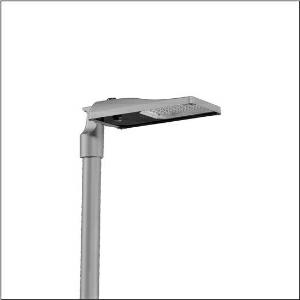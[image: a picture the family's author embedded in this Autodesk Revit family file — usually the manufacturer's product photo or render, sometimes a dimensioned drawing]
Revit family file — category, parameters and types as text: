
# Revit family: streetlight_sl_31_mini___st1_0a_5xh2d3at08ha_b443
name_source: partatom
category: Lighting Fixtures
units: mm (PartAtom-declared; Revit-internal decimal feet)

## family parameters
Cut with Voids When Loaded = No
Host = Face
Light Source = No
Part Type = Normal
Room Calculation Point = No
Round Connector Dimension = Use Diameter
Shared = No

## types (1)
- --- (1 x LED, 9230 lm, 68.3 W, 3000K)
    Apparent Load = 68 VA
    CIE Flux Codes = 37 72 97 100 100
    Color Rendering = 70
    Color Temperature = 3000K
    Default Elevation = 1800 mm
    Description = Streetlight SL 31 mini D4i mast luminaire for post-top, side-entry; light control with lens of PMMA; light distribution: ST1.0a, direct asymmetric distribution, for standard-compliant lighting for roads and squares; LED: luminous flux: 9.230lm, light colour: 730, colour temperature: 3000K; luminous efficacy: 135,1lm/W; control: pre-setting: logarithmic dimming characteristic, flexible luminous flux parameterisation, time-dependent luminous flux control, constant luminous flux control, power reduction, intelligent temperature release in ECG and LED module, overheat protection; luminaire housing, of diecast aluminium, SITECO metallic grey (DB 702S), corrosivity category C5 high according to DIN EN ISO 12944; cover of toughened safety glass, transparent, mast flange of diecast aluminium, SITECO metallic grey (DB 702S), spigot size: 76/60mm, mast flange included unmounted; cable length: 8,5m, connection cable pre-assembled; mains connection: 220..240V, AC, 50/60Hz; power consumption (at start of service life): 68,3W / (at end of service life): 74,5W / (with reduced operation 50%): 29,5W; protection rating (complete): IP66; insulation class (complete): insulation class II (safety insulation); impact resistance: IK09; certification: CE, ENEC, ENEC+, VDE, UKCA, ZD4i; permissible operating ambient temperature for outdoor applications: -40..+50°C; packaging unit: 1 piece

Light Distribution: ST1.0a
    Height = 76 mm
    Lamp = 1 x LED
    Lamp Light Flux = 9230 lm
    Lamp Power = 68.3 W
    Lamp count = 1
    Length = 547 mm
    Luminous efficacy = 135 lm/W
    Manufacturer = Siteco
    ModVariant = No
    Model = 5XH2D3AT08HA
    Number of Poles = 1
    OnlyDefault = Yes
    Power Factor = 1
    Product Name = Streetlight SL 31 mini | ST1.0a
    Product group = mast luminaire | pylon top
    ProductGroupID = 6100
    Protection Class = Protection class II
    Protection Degree = IP 66
    RLX_Detail_Level = 1
    RLX_Emergency_Light_Flux = 0 lm
    RLX_Emergency_Type = 0
    RLX_Emergency_Type_DB = No
    RlxData = <blob elided: 39553 chars, md5=8b69e2b0>
    Socket = socket
    Standby Power = 0 W
    System Light Flux = 9230 lm
    System Power = 68 W
    Type Comments = factory setting: luminous flux: 100 % | dim-lin: 254 | 692 mA
    Type Image = l_1300332.jpg
    URL = http://relux.com
    VarID = @adj_020549
    Voltage = 0 V
    Weight = 0.00 kg
    Width = 265 mm

## geometry (parser evidence)
native form markers: Blend x4, Sweep x10
no freeform markers — native parametric forms only
